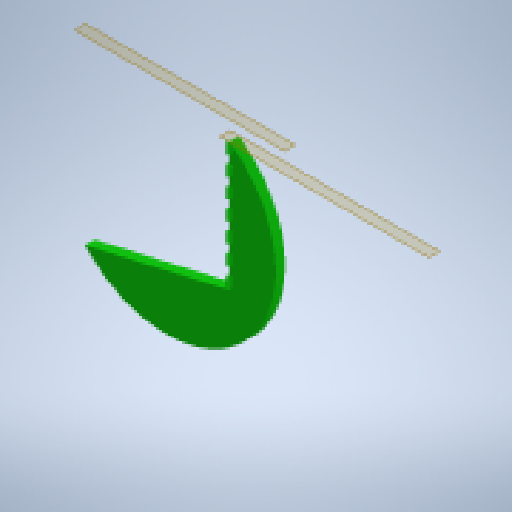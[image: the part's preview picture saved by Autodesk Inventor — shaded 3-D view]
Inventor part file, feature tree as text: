
AUTODESK INVENTOR PART (.ipt)
format: ipt  version: 2023 (Build 270158030, 158C)  size: 204,288 bytes
history: native  units: mm
features: other x5, plane x4, extrude x2, sketch x2, pattern_linear x1, reference x1
ambient origin geometry x8: Origin, YZ Plane, XZ Plane, XY Plane, X Axis, Y Axis, Z Axis, Center Point
bodies: Body1 (feature_tree)
feature tree (15):
  other  "side-flap"
  extrude  "Extrusion1"  Depth=30.0mm TaperAngle=0.0deg
  plane  "Work Plane3"
  plane  "Work Plane1"
  plane  "Work Plane4"
  extrude  "Extrusion2"  Depth=5.0mm
  pattern_linear  "Rectangular Pattern1"  Spacing1=1.0mm  [1 undecoded]
  sketch  "Sketch1"  dims[d0=340.0mm d1=30.0mm d2=0.0mm]
  reference  "Reference1"
  plane  "Work Plane2"
  sketch  "Sketch2"  dims[d3=10.0mm d4=5.0mm d5=1.0mm d6=1.5mm d9=5.0mm d11=5.0mm d12=10.0mm d13=10.0mm d14=6.0mm d15=4.0mm d16=30.0mm d17=0.0mm d18=70.0mm d20=60.0mm]
  other  "<userpath>\Documents\0004-inventor\3D-CAD-main\primary-engineer-bench.iam"
  other  "primary-engineer-bench.iam"
  other  "bench-end-peice:1"
  other  "backrest:1"
note: 1 required parameter value undecoded (feature->parameter linkage not recoverable at this tier; creation-order binding heuristic only, values carry confidence <= 0.55)
